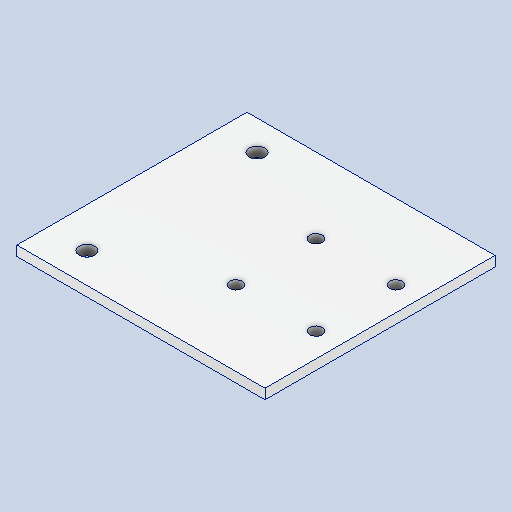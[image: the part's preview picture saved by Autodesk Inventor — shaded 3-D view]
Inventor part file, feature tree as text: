
AUTODESK INVENTOR PART (.ipt)
format: ipt  version: 2023 (Build 270158000, 158)  size: 110,080 bytes
history: native  units: in
note: dims shown in document units (in); Inventor stores cm internally (conversion verified against a paired STEP export)
features: other x3, sketch x2
ambient origin geometry x8: Origin, YZ Plane, XZ Plane, XY Plane, X Axis, Y Axis, Z Axis, Center Point
bodies: Solid1 (feature_tree)
feature tree (5):
  other  "MotorMount.ipt"
  other  "Solid1::MotorMount.ipt"
  other  "TaggingFeature1"
  sketch  "Sketch1"  dims[d0=0.3937in]
  sketch  "Sketch2"
